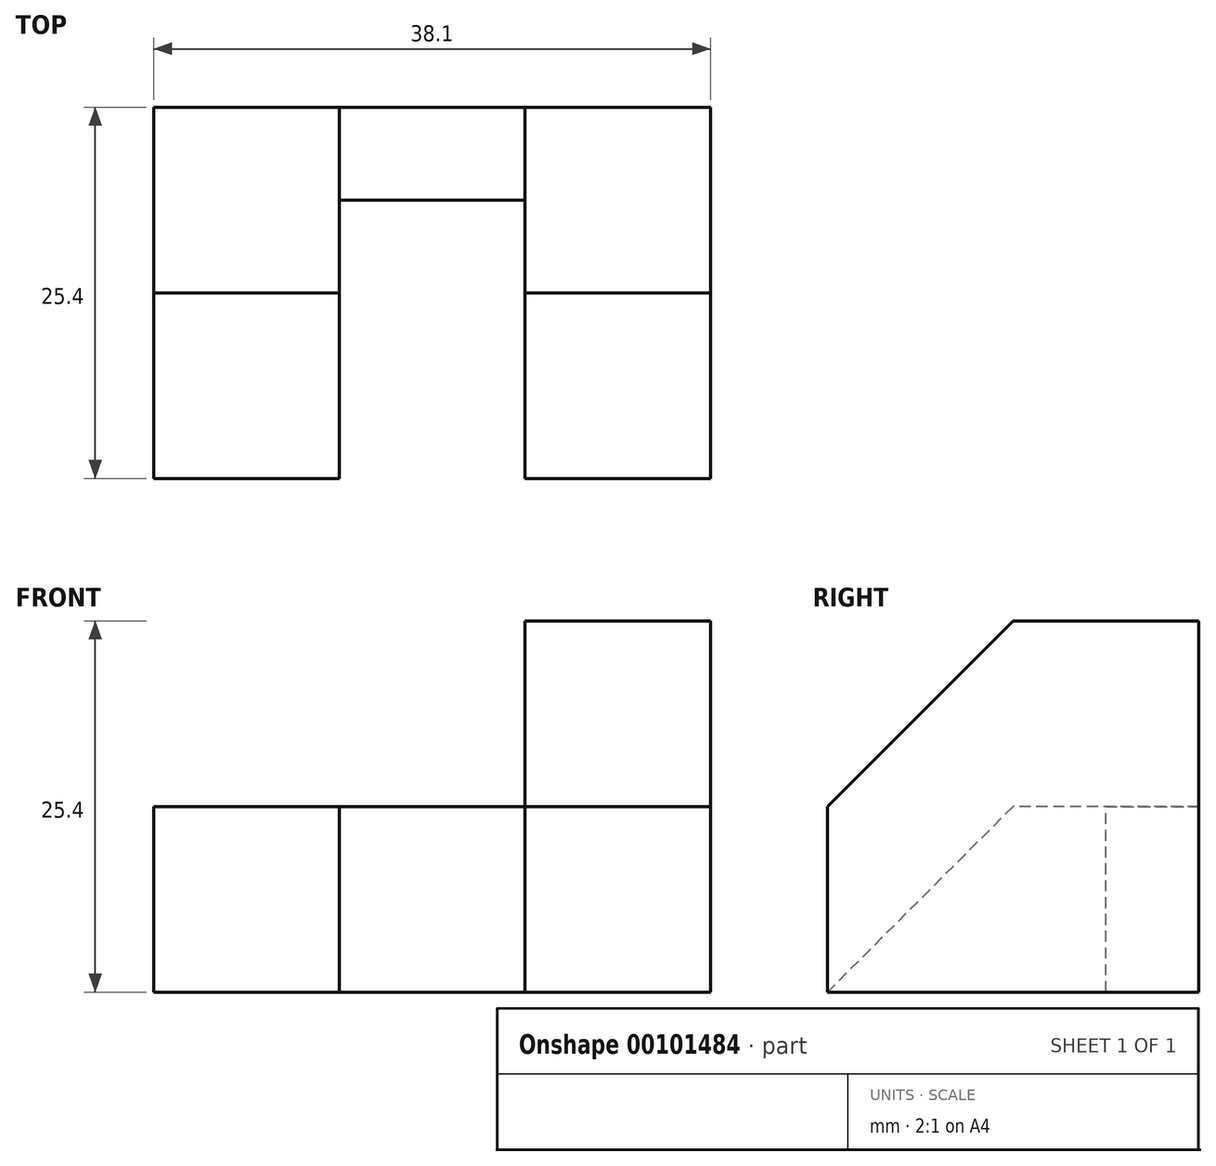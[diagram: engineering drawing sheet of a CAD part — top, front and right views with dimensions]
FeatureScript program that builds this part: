
annotation { "Feature Type Name" : "Feature", "Feature Type Description" : "" }
export const myFeature = defineFeature(function(context is Context, id is Id, definition is map)
    precondition{}
    {
        {
            var Q0;
            Q0=qCreatedBy(makeId("Right.planeOp"),FACE);
            var sketch = newSketch(context, id + "F0", { "sketchPlane" : qUnion([Q0])});
            skLineSegment(sketch, "E0", {"start": v(0, 0) * mm, "end": v(0, 25.4) * mm});
            skLineSegment(sketch, "E1", {"start": v(0, 25.4) * mm, "end": v(-12.7, 25.4) * mm});
            skLineSegment(sketch, "E2", {"start": v(-12.7, 25.4) * mm, "end": v(-25.4, 12.7) * mm});
            skLineSegment(sketch, "E3", {"start": v(-25.4, 12.7) * mm, "end": v(-25.4, 0) * mm});
            skLineSegment(sketch, "E4", {"start": v(-25.4, 0) * mm, "end": v(0, 0) * mm});
            skSolve(sketch);
        }
        {
            var Q0;
            Q0=makeQuery(id+"F0.imprint","IMPRINT",FACE,{"disambiguationData":[TD([[makeQuery(id+"F0.imprint","IMPRINT",EDGE,{"derivedFrom":sQuery(id+"F0.wireOp",EDGE,"E0")}),1.0]])]});
            extrude(context, id + "F1", {"entities" : qUnion([Q0]), "depth" : 12.7 * mm});
        }
        {
            var Q0;
            Q0=qCreatedBy(makeId("Front.planeOp"),FACE);
            var sketch = newSketch(context, id + "F2", { "sketchPlane" : qUnion([Q0])});
            skLineSegment(sketch, "E5", {"start": v(0, 0) * mm, "end": v(0, 12.7) * mm});
            skLineSegment(sketch, "E6", {"start": v(0, 12.7) * mm, "end": v(-12.7, 12.7) * mm});
            skLineSegment(sketch, "E7", {"start": v(-12.7, 12.7) * mm, "end": v(-12.7, 0) * mm});
            skLineSegment(sketch, "E8", {"start": v(-12.7, 0) * mm, "end": v(0, 0) * mm});
            skSolve(sketch);
        }
        {
            var Q0;
            Q0=makeQuery(id+"F2.imprint","IMPRINT",FACE,{"disambiguationData":[TD([[makeQuery(id+"F2.imprint","IMPRINT",EDGE,{"derivedFrom":sQuery(id+"F2.wireOp",EDGE,"E5")}),1.0]])]});
            extrude(context, id + "F3", {"entities" : qUnion([Q0]), "operationType" : NewBodyOperationType.ADD, "depth" : 6.35 * mm});
        }
        {
            var Q0;
            Q0=qCreatedBy(makeId("Right.planeOp"),FACE);
            var sketch = newSketch(context, id + "F4", { "sketchPlane" : qUnion([Q0])});
            skLineSegment(sketch, "E9", {"start": v(0, 0) * mm, "end": v(0, 12.7) * mm});
            skLineSegment(sketch, "E10", {"start": v(0, 12.7) * mm, "end": v(-12.7, 12.7) * mm});
            skLineSegment(sketch, "E11", {"start": v(-12.7, 12.7) * mm, "end": v(-25.4, 0) * mm});
            skLineSegment(sketch, "E12", {"start": v(-25.4, 0) * mm, "end": v(0, 0) * mm});
            skSolve(sketch);
        }
        {
            var Q0;
            Q0=makeQuery(id+"F4.imprint","IMPRINT",FACE,{"disambiguationData":[TD([[makeQuery(id+"F4.imprint","IMPRINT",EDGE,{"derivedFrom":sQuery(id+"F4.wireOp",EDGE,"E9")}),1.0]])]});
            extrude(context, id + "F5", {"entities" : qUnion([Q0]), "operationType" : NewBodyOperationType.ADD, "oppositeDirection" : true, "depth" : 25.4 * mm, "hasSecondDirection" : true, "secondDirectionOppositeDirection" : true, "secondDirectionDepth" : 12.7 * mm});
        }
    });
